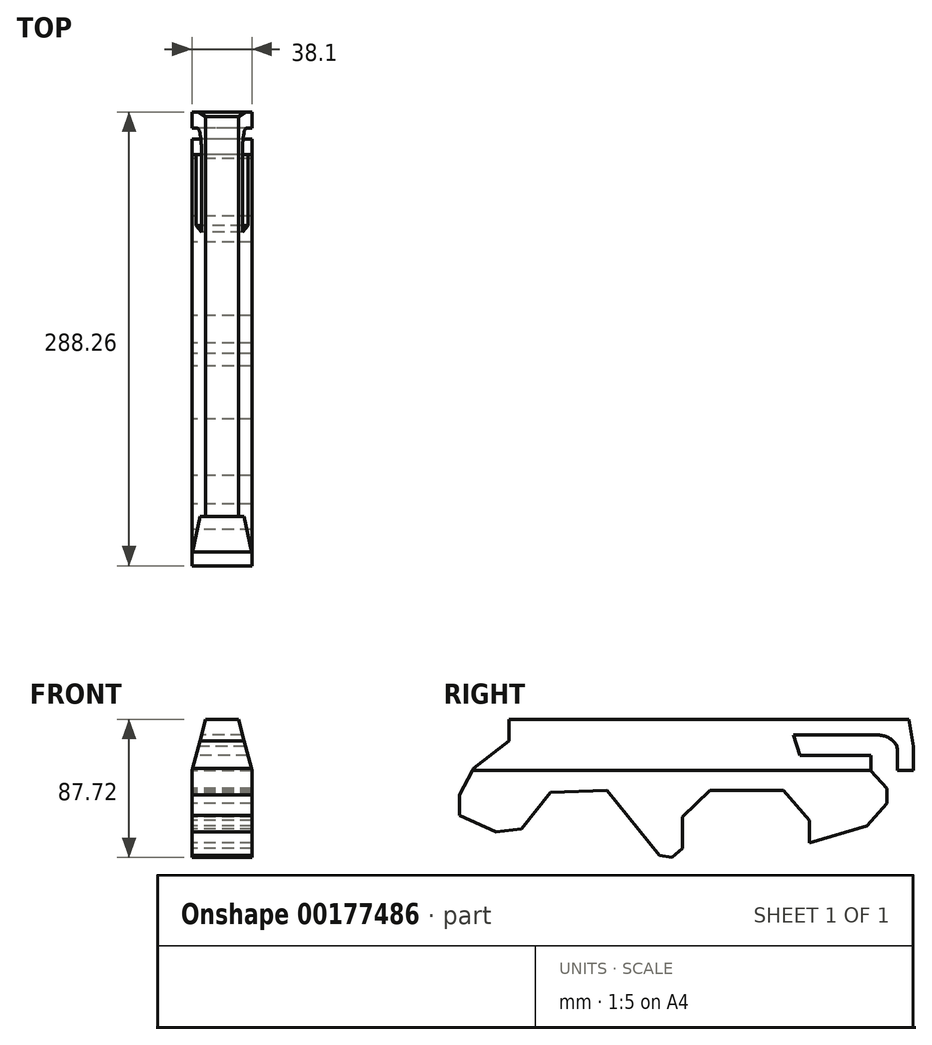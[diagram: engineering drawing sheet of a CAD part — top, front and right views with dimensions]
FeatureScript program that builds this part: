
annotation { "Feature Type Name" : "Feature", "Feature Type Description" : "" }
export const myFeature = defineFeature(function(context is Context, id is Id, definition is map)
    precondition{}
    {
        {
            var Q0;
            Q0=qCreatedBy(makeId("Right.planeOp"),FACE);
            var sketch = newSketch(context, id + "F0", { "sketchPlane" : qUnion([Q0])});
            skLineSegment(sketch, "E0", {"start": v(-123.23, 33.95) * mm, "end": v(130.77, 33.95) * mm});
            skLineSegment(sketch, "E1", {"start": v(130.77, 33.95) * mm, "end": v(133.7, 16.83) * mm});
            skLineSegment(sketch, "E2", {"start": v(133.7, 16.83) * mm, "end": v(133.7, 1.68) * mm});
            skLineSegment(sketch, "E3", {"start": v(133.7, 1.68) * mm, "end": v(123.39, 1.68) * mm});
            skLineSegment(sketch, "E4", {"start": v(123.39, 1.68) * mm, "end": v(123.39, 15.25) * mm});
            skLineSegment(sketch, "E5", {"start": v(107.53, 24.17) * mm, "end": v(57.32, 24.17) * mm});
            skLineSegment(sketch, "E6", {"start": v(57.32, 24.17) * mm, "end": v(61.7, 11.2) * mm});
            skLineSegment(sketch, "E7", {"start": v(61.7, 11.2) * mm, "end": v(106.83, 11.2) * mm});
            skLineSegment(sketch, "E8", {"start": v(106.83, 11.2) * mm, "end": v(106.83, 1.36) * mm});
            skLineSegment(sketch, "E9", {"start": v(106.83, 1.36) * mm, "end": v(116.67, -10.04) * mm});
            skLineSegment(sketch, "E10", {"start": v(116.67, -10.04) * mm, "end": v(116.67, -19.4) * mm});
            skLineSegment(sketch, "E11", {"start": v(116.67, -19.4) * mm, "end": v(104.18, -33.78) * mm});
            skLineSegment(sketch, "E12", {"start": v(104.18, -33.78) * mm, "end": v(67.63, -44.55) * mm});
            skLineSegment(sketch, "E13", {"start": v(67.63, -44.55) * mm, "end": v(67.63, -30.18) * mm});
            skLineSegment(sketch, "E14", {"start": v(67.63, -30.18) * mm, "end": v(51.23, -11.13) * mm});
            skLineSegment(sketch, "E15", {"start": v(51.23, -11.13) * mm, "end": v(4.53, -11.13) * mm});
            skLineSegment(sketch, "E16", {"start": v(4.53, -11.13) * mm, "end": v(-13.11, -28) * mm});
            skLineSegment(sketch, "E17", {"start": v(-13.11, -28) * mm, "end": v(-13.11, -47.99) * mm});
            skLineSegment(sketch, "E18", {"start": v(-13.11, -47.99) * mm, "end": v(-19.83, -53.77) * mm});
            skLineSegment(sketch, "E19", {"start": v(-19.83, -53.77) * mm, "end": v(-27.64, -52.52) * mm});
            skLineSegment(sketch, "E20", {"start": v(-27.64, -52.52) * mm, "end": v(-61.14, -11.13) * mm});
            skLineSegment(sketch, "E21", {"start": v(-61.14, -11.13) * mm, "end": v(-96.99, -12.44) * mm});
            skLineSegment(sketch, "E22", {"start": v(-96.99, -12.44) * mm, "end": v(-115.38, -35.47) * mm});
            skLineSegment(sketch, "E23", {"start": v(-115.38, -35.47) * mm, "end": v(-131.53, -37.51) * mm});
            skLineSegment(sketch, "E24", {"start": v(-131.53, -37.51) * mm, "end": v(-154.57, -26.92) * mm});
            skLineSegment(sketch, "E25", {"start": v(-154.57, -26.92) * mm, "end": v(-154.57, -14.1) * mm});
            skLineSegment(sketch, "E26", {"start": v(-154.57, -14.1) * mm, "end": v(-145.65, 2.98) * mm});
            skLineSegment(sketch, "E27", {"start": v(-145.65, 2.98) * mm, "end": v(-123.23, 20.44) * mm});
            skLineSegment(sketch, "E28", {"start": v(-123.23, 20.44) * mm, "end": v(-123.23, 33.95) * mm});
            skFitSpline(sketch, "E29", {"points": [v(123.39, 15.25) * mm, v(118.83, 21.71) * mm, v(107.53, 24.17) * mm], "startDerivative": vector(0, 17.57) * mm, "endDerivative": vector(-31.34, 0) * mm});
            skSolve(sketch);
        }
        {
            var Q0;
            Q0 = qSketchRegion(id + "F0", true);
            extrude(context, id + "F1", {"entities" : qUnion([Q0]), "endBound" : BoundingType.SYMMETRIC, "depth" : 38.1 * mm});
        }
        {
            var Q0;
            Q0=makeQuery(id+"F1.opExtrude","SWEPT_FACE",FACE,{"disambiguationData":[OSD([sQuery(id+"F0.wireOp",EDGE,"E2")])]});
            var sketch = newSketch(context, id + "F2", { "sketchPlane" : qUnion([Q0])});
            skLineSegment(sketch, "E30", {"start": v(-19.05, 1.68) * mm, "end": v(0, 72.77) * mm});
            skLineSegment(sketch, "E31", {"start": v(0, 72.77) * mm, "end": v(19.05, 1.68) * mm});
            skLineSegment(sketch, "E32", {"start": v(19.05, 1.68) * mm, "end": v(19.05, 77.07) * mm});
            skLineSegment(sketch, "E33", {"start": v(19.05, 77.07) * mm, "end": v(-19.05, 77.07) * mm});
            skLineSegment(sketch, "E34", {"start": v(-19.05, 77.07) * mm, "end": v(-19.05, 1.68) * mm});
            skSolve(sketch);
        }
        {
            var Q0;
            Q0 = qSketchRegion(id + "F2", true);
            extrude(context, id + "F3", {"entities" : qUnion([Q0]), "operationType" : NewBodyOperationType.REMOVE, "oppositeDirection" : true, "depth" : 329.18 * mm});
        }
    });
